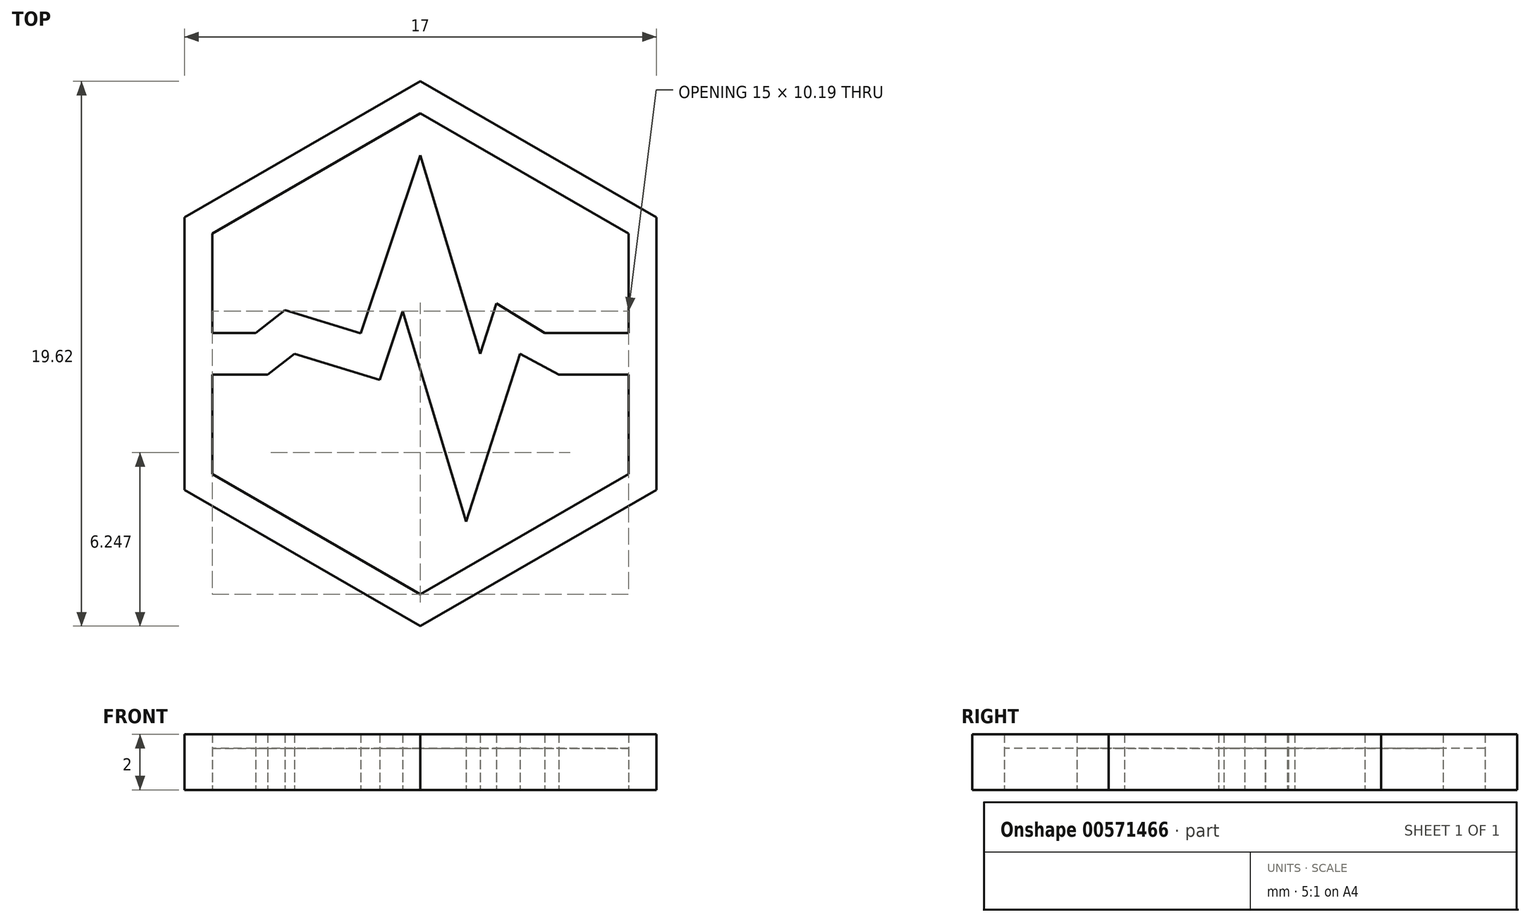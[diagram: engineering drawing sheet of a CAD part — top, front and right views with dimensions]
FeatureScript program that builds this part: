
annotation { "Feature Type Name" : "Feature", "Feature Type Description" : "" }
export const myFeature = defineFeature(function(context is Context, id is Id, definition is map)
    precondition{}
    {
        {
            var Q0;
            Q0=qCreatedBy(makeId("Top.planeOp"),FACE);
            var sketch = newSketch(context, id + "F0", { "sketchPlane" : qUnion([Q0])});
            skCircle(sketch, "E0.cCircle", {"center": v(0, 0) * mm, "radius": 8.5 * mm, "construction": true});
            skLineSegment(sketch, "E0.0", {"start": v(8.5, -4.9) * mm, "end": v(0, -9.81) * mm});
            skLineSegment(sketch, "E0.1", {"start": v(0, -9.81) * mm, "end": v(-8.5, -4.9) * mm});
            skLineSegment(sketch, "E0.2", {"start": v(-8.5, -4.9) * mm, "end": v(-8.5, 4.9) * mm});
            skLineSegment(sketch, "E0.3", {"start": v(-8.5, 4.9) * mm, "end": v(0, 9.81) * mm});
            skLineSegment(sketch, "E0.4", {"start": v(0, 9.81) * mm, "end": v(8.5, 4.9) * mm});
            skLineSegment(sketch, "E0.5", {"start": v(8.5, 4.9) * mm, "end": v(8.5, -4.9) * mm});
            skPoint(sketch, "E0.0.midPoint", {"position": v(4.25, -7.36) * mm});
            skCircle(sketch, "E1.cCircle", {"center": v(0, 0) * mm, "radius": 7.5 * mm, "construction": true});
            skLineSegment(sketch, "E1.0", {"start": v(7.5, -4.33) * mm, "end": v(0, -8.66) * mm});
            skLineSegment(sketch, "E1.1", {"start": v(0, -8.66) * mm, "end": v(-7.5, -4.33) * mm});
            skLineSegment(sketch, "E1.2", {"start": v(-7.5, -4.33) * mm, "end": v(-7.5, -0.75) * mm});
            skLineSegment(sketch, "E1.3", {"start": v(-7.5, 4.33) * mm, "end": v(0, 8.66) * mm});
            skLineSegment(sketch, "E1.4", {"start": v(0, 8.66) * mm, "end": v(7.5, 4.33) * mm});
            skLineSegment(sketch, "E1.5", {"start": v(7.5, 4.33) * mm, "end": v(7.5, 0.75) * mm});
            skPoint(sketch, "E1.0.midPoint", {"position": v(3.75, -6.5) * mm});
            skLineSegment(sketch, "E2", {"start": v(-7.5, 0.75) * mm, "end": v(-5.93, 0.75) * mm});
            skLineSegment(sketch, "E3", {"start": v(-5.93, 0.75) * mm, "end": v(-4.88, 1.57) * mm});
            skLineSegment(sketch, "E4", {"start": v(-4.88, 1.57) * mm, "end": v(-2.15, 0.73) * mm});
            skLineSegment(sketch, "E5", {"start": v(-2.15, 0.73) * mm, "end": v(0, 7.15) * mm});
            skLineSegment(sketch, "E6", {"start": v(0, 7.15) * mm, "end": v(2.15, 0) * mm});
            skLineSegment(sketch, "E7", {"start": v(2.15, 0) * mm, "end": v(2.73, 1.8) * mm});
            skLineSegment(sketch, "E8", {"start": v(2.73, 1.8) * mm, "end": v(4.48, 0.75) * mm});
            skLineSegment(sketch, "E9", {"start": v(4.48, 0.75) * mm, "end": v(7.5, 0.75) * mm});
            skLineSegment(sketch, "E10", {"start": v(-7.5, -0.75) * mm, "end": v(-5.5, -0.75) * mm});
            skLineSegment(sketch, "E11", {"start": v(-5.5, -0.75) * mm, "end": v(-4.54, 0) * mm});
            skLineSegment(sketch, "E12", {"start": v(-4.54, 0) * mm, "end": v(-1.47, -0.94) * mm});
            skLineSegment(sketch, "E13", {"start": v(-1.47, -0.94) * mm, "end": v(-0.64, 1.53) * mm});
            skLineSegment(sketch, "E14", {"start": v(-0.64, 1.53) * mm, "end": v(1.65, -6.05) * mm});
            skLineSegment(sketch, "E15", {"start": v(1.65, -6.05) * mm, "end": v(3.59, 0) * mm});
            skLineSegment(sketch, "E16", {"start": v(3.59, 0) * mm, "end": v(4.98, -0.75) * mm});
            skLineSegment(sketch, "E17", {"start": v(4.98, -0.75) * mm, "end": v(7.5, -0.75) * mm});
            skLineSegment(sketch, "E18.trimOffspring", {"start": v(-7.5, 0.75) * mm, "end": v(-7.5, 4.33) * mm});
            skLineSegment(sketch, "E19.trimOffspring", {"start": v(7.5, -0.75) * mm, "end": v(7.5, -4.33) * mm});
            skSolve(sketch);
        }
        {
            var Q0;
            Q0=makeQuery(id+"F0.imprint","IMPRINT",FACE,{"disambiguationData":[TD([[makeQuery(id+"F0.imprint","IMPRINT",EDGE,{"derivedFrom":sQuery(id+"F0.wireOp",EDGE,"E0.0")}),-1.0]])]});
            extrude(context, id + "F1", {"entities" : qUnion([Q0]), "depth" : 2 * mm});
        }
        {
            var Q0;
            Q0=makeQuery(id+"F0.imprint","IMPRINT",FACE,{"disambiguationData":[TD([[makeQuery(id+"F0.imprint","IMPRINT",EDGE,{"derivedFrom":sQuery(id+"F0.wireOp",EDGE,"E1.3")}),-1.0]])]});
            var Q1;
            Q1=makeQuery(id+"F0.imprint","IMPRINT",FACE,{"disambiguationData":[TD([[makeQuery(id+"F0.imprint","IMPRINT",EDGE,{"derivedFrom":sQuery(id+"F0.wireOp",EDGE,"E1.0")}),-1.0]])]});
            extrude(context, id + "F2", {"entities" : qUnion([Q0, Q1]), "depth" : 1.5 * mm});
        }
    });
